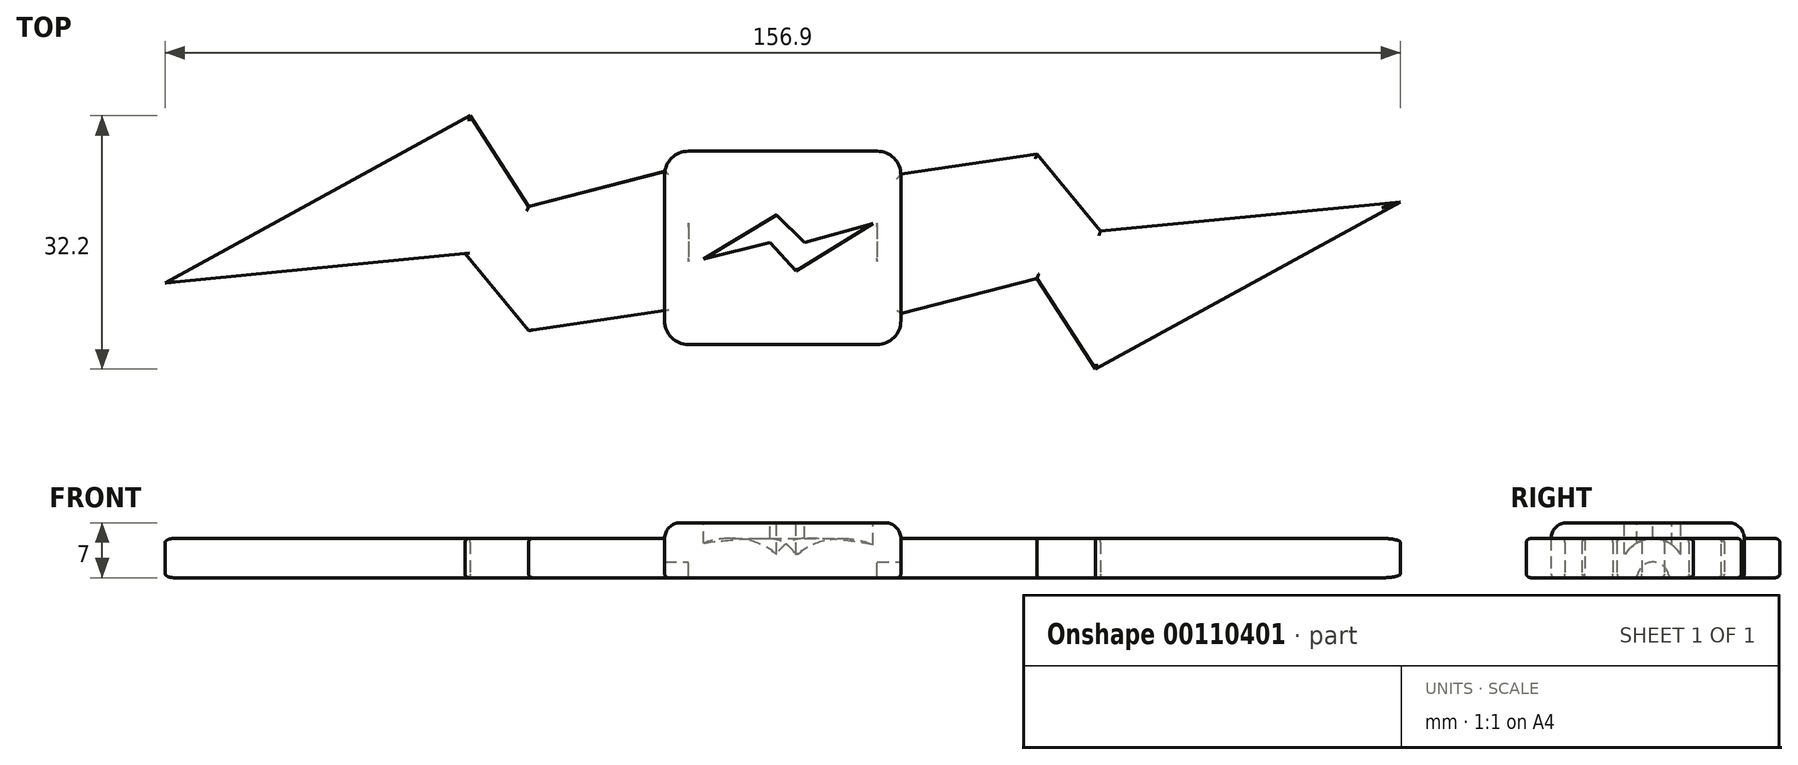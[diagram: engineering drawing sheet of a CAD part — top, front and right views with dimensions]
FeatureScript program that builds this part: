
annotation { "Feature Type Name" : "Feature", "Feature Type Description" : "" }
export const myFeature = defineFeature(function(context is Context, id is Id, definition is map)
    precondition{}
    {
        {
            var Q0;
            Q0=qCreatedBy(makeId("Top.planeOp"),FACE);
            var sketch = newSketch(context, id + "F0", { "sketchPlane" : qUnion([Q0])});
            skLineSegment(sketch, "E0.bottom", {"start": v(0, 11.6) * mm, "end": v(-15, 11.6) * mm});
            skLineSegment(sketch, "E0.top", {"start": v(0, -12.95) * mm, "end": v(-15, -12.95) * mm});
            skLineSegment(sketch, "E0.left", {"start": v(0, 11.6) * mm, "end": v(0, -12.95) * mm});
            skLineSegment(sketch, "E0.right", {"start": v(-15, 11.6) * mm, "end": v(-15, -12.95) * mm});
            skLineSegment(sketch, "E1", {"start": v(-78.45, -5.13) * mm, "end": v(-39.7, 16.1) * mm});
            skLineSegment(sketch, "E2", {"start": v(-39.7, 16.1) * mm, "end": v(-32.29, 4.57) * mm});
            skLineSegment(sketch, "E3", {"start": v(-32.29, 4.57) * mm, "end": v(-15, 9.02) * mm});
            skLineSegment(sketch, "E4", {"start": v(-15, 11.6) * mm, "end": v(-15, 9.02) * mm});
            skLineSegment(sketch, "E5", {"start": v(-78.45, -5.13) * mm, "end": v(-40.38, -1.43) * mm});
            skLineSegment(sketch, "E6", {"start": v(-40.38, -1.43) * mm, "end": v(-32.29, -11.2) * mm});
            skLineSegment(sketch, "E7", {"start": v(-32.29, -11.2) * mm, "end": v(-15, -8.67) * mm});
            skLineSegment(sketch, "E8.MirrorCS", {"start": v(0, -12.95) * mm, "end": v(15, -12.95) * mm});
            skLineSegment(sketch, "E9.MirrorCS", {"start": v(15, 11.6) * mm, "end": v(15, -12.95) * mm});
            skLineSegment(sketch, "E10", {"start": v(0, 0) * mm, "end": v(18.95, 0) * mm, "construction": true});
            skLineSegment(sketch, "E11.MirrorCS", {"start": v(40.38, 1.43) * mm, "end": v(32.29, 11.2) * mm});
            skLineSegment(sketch, "E12.MirrorCS", {"start": v(78.45, 5.13) * mm, "end": v(40.38, 1.43) * mm});
            skLineSegment(sketch, "E13.MirrorCS", {"start": v(32.29, -4.57) * mm, "end": v(15, -9.02) * mm});
            skLineSegment(sketch, "E14.MirrorCS", {"start": v(39.7, -16.1) * mm, "end": v(32.29, -4.57) * mm});
            skLineSegment(sketch, "E15.MirrorCS", {"start": v(78.45, 5.13) * mm, "end": v(39.7, -16.1) * mm});
            skLineSegment(sketch, "E16.MirrorCS", {"start": v(32.29, 11.2) * mm, "end": v(15, 8.67) * mm});
            skLineSegment(sketch, "E17", {"start": v(0, 11.6) * mm, "end": v(15, 11.6) * mm});
            skSolve(sketch);
        }
        {
            var Q0;
            Q0 = qSketchRegion(id + "F0", true);
            extrude(context, id + "F1", {"entities" : qUnion([Q0]), "depth" : 5 * mm});
        }
        {
            var Q0;
            Q0=makeQuery(id+"F1.opExtrude","CAP_FACE",FACE,{"disambiguationData":[OSD([sQuery(id+"F0.wireOp",EDGE,"E8.MirrorCS"),sQuery(id+"F0.wireOp",EDGE,"E9.MirrorCS"),sQuery(id+"F0.wireOp",EDGE,"E6"),sQuery(id+"F0.wireOp",EDGE,"E5"),sQuery(id+"F0.wireOp",EDGE,"E3"),sQuery(id+"F0.wireOp",EDGE,"E0.bottom"),sQuery(id+"F0.wireOp",EDGE,"E0.right"),sQuery(id+"F0.wireOp",EDGE,"E7"),sQuery(id+"F0.wireOp",EDGE,"E2"),sQuery(id+"F0.wireOp",EDGE,"E0.top"),sQuery(id+"F0.wireOp",EDGE,"E1"),sQuery(id+"F0.wireOp",EDGE,"E11.MirrorCS"),sQuery(id+"F0.wireOp",EDGE,"E12.MirrorCS"),sQuery(id+"F0.wireOp",EDGE,"E13.MirrorCS"),sQuery(id+"F0.wireOp",EDGE,"E14.MirrorCS"),sQuery(id+"F0.wireOp",EDGE,"E15.MirrorCS"),sQuery(id+"F0.wireOp",EDGE,"E16.MirrorCS"),sQuery(id+"F0.wireOp",EDGE,"E17")])],"isStart":false});
            var sketch = newSketch(context, id + "F2", { "sketchPlane" : qUnion([Q0])});
            skLineSegment(sketch, "E18.bottom", {"start": v(-15, 11.6) * mm, "end": v(15, 11.6) * mm});
            skLineSegment(sketch, "E18.top", {"start": v(-15, -12.95) * mm, "end": v(15, -12.95) * mm});
            skLineSegment(sketch, "E18.left", {"start": v(-15, 11.6) * mm, "end": v(-15, -12.95) * mm});
            skLineSegment(sketch, "E18.right", {"start": v(15, 11.6) * mm, "end": v(15, -12.95) * mm});
            skSolve(sketch);
        }
        {
            var Q0;
            Q0 = qSketchRegion(id + "F2", true);
            extrude(context, id + "F3", {"entities" : qUnion([Q0]), "operationType" : NewBodyOperationType.ADD, "depth" : 2 * mm});
        }
        {
            var Q0;
            Q0=makeQuery(id+"F3.boolean.opBoolean","MERGE",EDGE,{"derivedFrom":[makeQuery(id+"F1.opExtrude","SWEPT_EDGE",EDGE,{"disambiguationData":[OSD([sQuery(id+"F0.wireOp",EDGE,"E0.bottom"),sQuery(id+"F0.wireOp",EDGE,"E0.right")])]}),makeQuery(id+"F3.opExtrude","SWEPT_EDGE",EDGE,{"disambiguationData":[OSD([sQuery(id+"F2.wireOp",EDGE,"E18.bottom"),sQuery(id+"F2.wireOp",EDGE,"E18.left")])]})]});
            var Q1;
            Q1=makeQuery(id+"F3.boolean.opBoolean","MERGE",EDGE,{"derivedFrom":[makeQuery(id+"F1.opExtrude","SWEPT_EDGE",EDGE,{"disambiguationData":[OSD([sQuery(id+"F0.wireOp",EDGE,"E9.MirrorCS"),sQuery(id+"F0.wireOp",EDGE,"E17")])]}),makeQuery(id+"F3.opExtrude","SWEPT_EDGE",EDGE,{"disambiguationData":[OSD([sQuery(id+"F2.wireOp",EDGE,"E18.bottom"),sQuery(id+"F2.wireOp",EDGE,"E18.right")])]})]});
            var Q2;
            Q2=makeQuery(id+"F3.boolean.opBoolean","MERGE",EDGE,{"derivedFrom":[makeQuery(id+"F1.opExtrude","SWEPT_EDGE",EDGE,{"disambiguationData":[OSD([sQuery(id+"F0.wireOp",EDGE,"E0.right"),sQuery(id+"F0.wireOp",EDGE,"E0.top")])]}),makeQuery(id+"F3.opExtrude","SWEPT_EDGE",EDGE,{"disambiguationData":[OSD([sQuery(id+"F2.wireOp",EDGE,"E18.top"),sQuery(id+"F2.wireOp",EDGE,"E18.left")])]})]});
            var Q3;
            Q3=makeQuery(id+"F3.boolean.opBoolean","MERGE",EDGE,{"derivedFrom":[makeQuery(id+"F1.opExtrude","SWEPT_EDGE",EDGE,{"disambiguationData":[OSD([sQuery(id+"F0.wireOp",EDGE,"E8.MirrorCS"),sQuery(id+"F0.wireOp",EDGE,"E9.MirrorCS")])]}),makeQuery(id+"F3.opExtrude","SWEPT_EDGE",EDGE,{"disambiguationData":[OSD([sQuery(id+"F2.wireOp",EDGE,"E18.top"),sQuery(id+"F2.wireOp",EDGE,"E18.right")])]})]});
            fillet(context, id + "F4", {"entities" : qUnion([Q0, Q1, Q2, Q3]), "radius" : 3 * mm, "tangentPropagation" : true, "allowEdgeOverflow" : false});
        }
        {
            var Q0;
            Q0=makeQuery(id+"F3.opExtrude","CAP_EDGE",EDGE,{"disambiguationData":[OSD([sQuery(id+"F2.wireOp",EDGE,"E18.bottom")])],"isStart":false});
            fillet(context, id + "F5", {"entities" : qUnion([Q0]), "radius" : 2 * mm, "tangentPropagation" : true, "allowEdgeOverflow" : false});
        }
        {
            var Q0;
            Q0=makeQuery(id+"F3.opExtrude","CAP_FACE",FACE,{"disambiguationData":[OSD([sQuery(id+"F2.wireOp",EDGE,"E18.bottom"),sQuery(id+"F2.wireOp",EDGE,"E18.top"),sQuery(id+"F2.wireOp",EDGE,"E18.left"),sQuery(id+"F2.wireOp",EDGE,"E18.right")])],"isStart":false});
            var sketch = newSketch(context, id + "F6", { "sketchPlane" : qUnion([Q0])});
            skLineSegment(sketch, "E19", {"start": v(-10.1, -2.1) * mm, "end": v(-0.82, 3.5) * mm});
            skLineSegment(sketch, "E20", {"start": v(-0.82, 3.5) * mm, "end": v(2.75, 0) * mm});
            skLineSegment(sketch, "E21", {"start": v(2.75, 0) * mm, "end": v(11.47, 2.4) * mm});
            skLineSegment(sketch, "E22", {"start": v(11.47, 2.4) * mm, "end": v(1.7, -3.63) * mm});
            skLineSegment(sketch, "E23", {"start": v(1.7, -3.63) * mm, "end": v(-1.64, 0) * mm});
            skLineSegment(sketch, "E24", {"start": v(-1.64, 0) * mm, "end": v(-10.1, -2.1) * mm});
            skSolve(sketch);
        }
        {
            var Q0;
            Q0 = qSketchRegion(id + "F6", true);
            extrude(context, id + "F7", {"entities" : qUnion([Q0]), "operationType" : NewBodyOperationType.REMOVE, "oppositeDirection" : true, "depth" : 4 * mm});
        }
        {
            var Q0;
            Q0=makeQuery(id+"F1.opExtrude","CAP_FACE",FACE,{"disambiguationData":[OSD([sQuery(id+"F0.wireOp",EDGE,"E8.MirrorCS"),sQuery(id+"F0.wireOp",EDGE,"E9.MirrorCS"),sQuery(id+"F0.wireOp",EDGE,"E6"),sQuery(id+"F0.wireOp",EDGE,"E5"),sQuery(id+"F0.wireOp",EDGE,"E3"),sQuery(id+"F0.wireOp",EDGE,"E0.bottom"),sQuery(id+"F0.wireOp",EDGE,"E0.right"),sQuery(id+"F0.wireOp",EDGE,"E7"),sQuery(id+"F0.wireOp",EDGE,"E2"),sQuery(id+"F0.wireOp",EDGE,"E0.top"),sQuery(id+"F0.wireOp",EDGE,"E1"),sQuery(id+"F0.wireOp",EDGE,"E11.MirrorCS"),sQuery(id+"F0.wireOp",EDGE,"E12.MirrorCS"),sQuery(id+"F0.wireOp",EDGE,"E13.MirrorCS"),sQuery(id+"F0.wireOp",EDGE,"E14.MirrorCS"),sQuery(id+"F0.wireOp",EDGE,"E15.MirrorCS"),sQuery(id+"F0.wireOp",EDGE,"E16.MirrorCS"),sQuery(id+"F0.wireOp",EDGE,"E17")])],"isStart":true});
            var sketch = newSketch(context, id + "F8", { "sketchPlane" : qUnion([Q0])});
            skLineSegment(sketch, "E25.bottom", {"start": v(15, -4) * mm, "end": v(12, -4) * mm});
            skLineSegment(sketch, "E25.top", {"start": v(15, 4) * mm, "end": v(12, 4) * mm});
            skLineSegment(sketch, "E25.left", {"start": v(15, -4) * mm, "end": v(15, 4) * mm});
            skLineSegment(sketch, "E25.right", {"start": v(12, -4) * mm, "end": v(12, 4) * mm});
            skLineSegment(sketch, "E26", {"start": v(0, 0) * mm, "end": v(0, -6.2) * mm, "construction": true});
            skLineSegment(sketch, "E27.MirrorCS", {"start": v(-15, -4) * mm, "end": v(-12, -4) * mm});
            skLineSegment(sketch, "E28.MirrorCS", {"start": v(-15, -4) * mm, "end": v(-15, 4) * mm});
            skLineSegment(sketch, "E29.MirrorCS", {"start": v(-12, -4) * mm, "end": v(-12, 4) * mm});
            skLineSegment(sketch, "E30.MirrorCS", {"start": v(-15, 4) * mm, "end": v(-12, 4) * mm});
            skSolve(sketch);
        }
        {
            var Q0;
            Q0 = qSketchRegion(id + "F8", true);
            extrude(context, id + "F9", {"entities" : qUnion([Q0]), "operationType" : NewBodyOperationType.REMOVE, "oppositeDirection" : true, "depth" : 5 * mm});
        }
        {
            var Q0;
            Q0=makeQuery(id+"F9.boolean.opBoolean","COPY",EDGE,{"derivedFrom":makeQuery(id+"F9.opExtrude","CAP_EDGE",EDGE,{"disambiguationData":[OSD([sQuery(id+"F8.wireOp",EDGE,"E25.bottom")])],"isStart":false})});
            var Q1;
            Q1=makeQuery(id+"F9.boolean.opBoolean","COPY",EDGE,{"derivedFrom":makeQuery(id+"F9.opExtrude","CAP_EDGE",EDGE,{"disambiguationData":[OSD([sQuery(id+"F8.wireOp",EDGE,"E25.top")])],"isStart":false})});
            var Q2;
            Q2=makeQuery(id+"F9.boolean.opBoolean","COPY",EDGE,{"derivedFrom":makeQuery(id+"F9.opExtrude","CAP_EDGE",EDGE,{"disambiguationData":[OSD([sQuery(id+"F8.wireOp",EDGE,"E30.MirrorCS")])],"isStart":false})});
            var Q3;
            Q3=makeQuery(id+"F9.boolean.opBoolean","COPY",EDGE,{"derivedFrom":makeQuery(id+"F9.opExtrude","CAP_EDGE",EDGE,{"disambiguationData":[OSD([sQuery(id+"F8.wireOp",EDGE,"E27.MirrorCS")])],"isStart":false})});
            fillet(context, id + "F10", {"entities" : qUnion([Q0, Q1, Q2, Q3]), "radius" : 4 * mm, "tangentPropagation" : true, "allowEdgeOverflow" : false});
        }
        {
            var Q0;
            Q0=makeQuery(id+"F9.boolean.opBoolean","COPY",FACE,{"derivedFrom":makeQuery(id+"F9.opExtrude","SWEPT_FACE",FACE,{"disambiguationData":[OSD([sQuery(id+"F8.wireOp",EDGE,"E25.left")])]})});
            var sketch = newSketch(context, id + "F11", { "sketchPlane" : qUnion([Q0])});
            skArc(sketch, "E31", {"start": v(-2, 0) * mm, "mid": v(0, 2) * mm, "end": v(2, 0) * mm});
            skSolve(sketch);
        }
        {
            var Q0;
            {var subQ0=sQuery(id+"F11.wireOp",EDGE,"E31");Q0=makeQuery(id+"F11.imprint","IMPRINT",FACE,{"disambiguationData":[TD([[makeQuery(id+"F11.imprint","IMPRINT",EDGE,{"derivedFrom":subQ0}),-1.0]])]});}
            var Q1;
            Q1=makeQuery(id+"F9.boolean.opBoolean","COPY",FACE,{"derivedFrom":makeQuery(id+"F9.opExtrude","SWEPT_FACE",FACE,{"disambiguationData":[OSD([sQuery(id+"F8.wireOp",EDGE,"E28.MirrorCS")])]})});
            extrude(context, id + "F12", {"entities" : qUnion([Q0]), "operationType" : NewBodyOperationType.ADD, "endBound" : BoundingType.UP_TO_SURFACE, "endBoundEntityFace" : qUnion([Q1]), "depth" : 25 * mm});
        }
        {
            var Q0;
            Q0=makeQuery(id+"F1.opExtrude","CAP_EDGE",EDGE,{"disambiguationData":[OSD([sQuery(id+"F0.wireOp",EDGE,"E7")])],"isStart":true});
            var Q1;
            Q1=makeQuery(id+"F1.opExtrude","CAP_EDGE",EDGE,{"disambiguationData":[OSD([sQuery(id+"F0.wireOp",EDGE,"E6")])],"isStart":true});
            var Q2;
            Q2=makeQuery(id+"F1.opExtrude","CAP_EDGE",EDGE,{"disambiguationData":[OSD([sQuery(id+"F0.wireOp",EDGE,"E5")])],"isStart":true});
            var Q3;
            Q3=makeQuery(id+"F1.opExtrude","CAP_EDGE",EDGE,{"disambiguationData":[OSD([sQuery(id+"F0.wireOp",EDGE,"E1")])],"isStart":true});
            var Q4;
            Q4=makeQuery(id+"F1.opExtrude","CAP_EDGE",EDGE,{"disambiguationData":[OSD([sQuery(id+"F0.wireOp",EDGE,"E2")])],"isStart":true});
            var Q5;
            Q5=makeQuery(id+"F1.opExtrude","CAP_EDGE",EDGE,{"disambiguationData":[OSD([sQuery(id+"F0.wireOp",EDGE,"E3")])],"isStart":true});
            var Q6;
            Q6=makeQuery(id+"F1.opExtrude","CAP_EDGE",EDGE,{"disambiguationData":[OSD([sQuery(id+"F0.wireOp",EDGE,"E8.MirrorCS"),sQuery(id+"F0.wireOp",EDGE,"E0.top")])],"isStart":true});
            var Q7;
            Q7=makeQuery(id+"F1.opExtrude","CAP_EDGE",EDGE,{"disambiguationData":[OSD([sQuery(id+"F0.wireOp",EDGE,"E0.bottom"),sQuery(id+"F0.wireOp",EDGE,"E17")])],"isStart":true});
            var Q8;
            Q8=makeQuery(id+"F1.opExtrude","CAP_EDGE",EDGE,{"disambiguationData":[OSD([sQuery(id+"F0.wireOp",EDGE,"E13.MirrorCS")])],"isStart":true});
            var Q9;
            Q9=makeQuery(id+"F1.opExtrude","CAP_EDGE",EDGE,{"disambiguationData":[OSD([sQuery(id+"F0.wireOp",EDGE,"E16.MirrorCS")])],"isStart":true});
            var Q10;
            Q10=makeQuery(id+"F1.opExtrude","CAP_EDGE",EDGE,{"disambiguationData":[OSD([sQuery(id+"F0.wireOp",EDGE,"E14.MirrorCS")])],"isStart":true});
            var Q11;
            Q11=makeQuery(id+"F1.opExtrude","CAP_EDGE",EDGE,{"disambiguationData":[OSD([sQuery(id+"F0.wireOp",EDGE,"E11.MirrorCS")])],"isStart":true});
            var Q12;
            Q12=makeQuery(id+"F1.opExtrude","CAP_EDGE",EDGE,{"disambiguationData":[OSD([sQuery(id+"F0.wireOp",EDGE,"E15.MirrorCS")])],"isStart":true});
            var Q13;
            Q13=makeQuery(id+"F1.opExtrude","CAP_EDGE",EDGE,{"disambiguationData":[OSD([sQuery(id+"F0.wireOp",EDGE,"E12.MirrorCS")])],"isStart":true});
            fillet(context, id + "F13", {"entities" : qUnion([Q0, Q1, Q2, Q3, Q4, Q5, Q6, Q7, Q8, Q9, Q10, Q11, Q12, Q13]), "radius" : 0.5 * mm, "tangentPropagation" : true, "allowEdgeOverflow" : false});
        }
        {
            var Q0;
            {var subQ0=sQuery(id+"F8.wireOp",EDGE,"E28.MirrorCS");Q0=makeQuery(id+"F12.boolean.opBoolean","SPLIT",EDGE,{"disambiguationData":[TD([makeQuery(id+"F9.boolean.opBoolean","COPY",FACE,{"derivedFrom":makeQuery(id+"F9.opExtrude","SWEPT_FACE",FACE,{"disambiguationData":[OSD([sQuery(id+"F8.wireOp",EDGE,"E30.MirrorCS")])]})})])],"derivedFrom":makeQuery(id+"F9.boolean.opBoolean","COPY",EDGE,{"derivedFrom":makeQuery(id+"F9.opExtrude","CAP_EDGE",EDGE,{"disambiguationData":[OSD([subQ0])],"isStart":true})})});}
            var Q1;
            {var subQ0=sQuery(id+"F11.wireOp",EDGE,"E31");var subQ1=sQuery(id+"F8.wireOp",EDGE,"E25.left");Q1=makeQuery(id+"F12.boolean.opBoolean","SPLIT",EDGE,{"disambiguationData":[TD([makeQuery(id+"F9.boolean.opBoolean","COPY",FACE,{"derivedFrom":makeQuery(id+"F9.opExtrude","SWEPT_FACE",FACE,{"disambiguationData":[OSD([sQuery(id+"F8.wireOp",EDGE,"E28.MirrorCS")])]})})])],"derivedFrom":makeQuery(id+"F12.opExtrude","SWEPT_EDGE",EDGE,{"disambiguationData":[OSD([subQ1,subQ0]),TDD([makeQuery(id+"F11.imprint","INTERSECT",VERTEX,{"disambiguationData":[OD(1.0)],"derivedFrom":[makeQuery(id+"F9.boolean.opBoolean","COPY",EDGE,{"derivedFrom":makeQuery(id+"F9.opExtrude","CAP_EDGE",EDGE,{"disambiguationData":[OSD([subQ1])],"isStart":true})}),subQ0]})])]})});}
            var Q2;
            {var subQ0=sQuery(id+"F8.wireOp",EDGE,"E29.MirrorCS");Q2=makeQuery(id+"F12.boolean.opBoolean","SPLIT",EDGE,{"disambiguationData":[TD([makeQuery(id+"F9.boolean.opBoolean","COPY",FACE,{"derivedFrom":makeQuery(id+"F9.opExtrude","SWEPT_FACE",FACE,{"disambiguationData":[OSD([sQuery(id+"F8.wireOp",EDGE,"E30.MirrorCS")])]})})])],"derivedFrom":makeQuery(id+"F9.boolean.opBoolean","COPY",EDGE,{"derivedFrom":makeQuery(id+"F9.opExtrude","CAP_EDGE",EDGE,{"disambiguationData":[OSD([subQ0])],"isStart":true})})});}
            var Q3;
            Q3=makeQuery(id+"F9.boolean.opBoolean","COPY",EDGE,{"derivedFrom":makeQuery(id+"F9.opExtrude","CAP_EDGE",EDGE,{"disambiguationData":[OSD([sQuery(id+"F8.wireOp",EDGE,"E30.MirrorCS")])],"isStart":true})});
            var Q4;
            {var subQ0=sQuery(id+"F11.wireOp",EDGE,"E31");var subQ1=sQuery(id+"F8.wireOp",EDGE,"E25.left");Q4=makeQuery(id+"F12.boolean.opBoolean","SPLIT",EDGE,{"disambiguationData":[TD([makeQuery(id+"F9.boolean.opBoolean","COPY",FACE,{"derivedFrom":makeQuery(id+"F9.opExtrude","SWEPT_FACE",FACE,{"disambiguationData":[OSD([sQuery(id+"F8.wireOp",EDGE,"E28.MirrorCS")])]})})])],"derivedFrom":makeQuery(id+"F12.opExtrude","SWEPT_EDGE",EDGE,{"disambiguationData":[OSD([subQ1,subQ0]),TDD([makeQuery(id+"F11.imprint","INTERSECT",VERTEX,{"disambiguationData":[OD(0.0)],"derivedFrom":[makeQuery(id+"F9.boolean.opBoolean","COPY",EDGE,{"derivedFrom":makeQuery(id+"F9.opExtrude","CAP_EDGE",EDGE,{"disambiguationData":[OSD([subQ1])],"isStart":true})}),subQ0]})])]})});}
            var Q5;
            {var subQ0=sQuery(id+"F8.wireOp",EDGE,"E28.MirrorCS");Q5=makeQuery(id+"F12.boolean.opBoolean","SPLIT",EDGE,{"disambiguationData":[TD([makeQuery(id+"F9.boolean.opBoolean","COPY",FACE,{"derivedFrom":makeQuery(id+"F9.opExtrude","SWEPT_FACE",FACE,{"disambiguationData":[OSD([sQuery(id+"F8.wireOp",EDGE,"E27.MirrorCS")])]})})])],"derivedFrom":makeQuery(id+"F9.boolean.opBoolean","COPY",EDGE,{"derivedFrom":makeQuery(id+"F9.opExtrude","CAP_EDGE",EDGE,{"disambiguationData":[OSD([subQ0])],"isStart":true})})});}
            var Q6;
            Q6=makeQuery(id+"F9.boolean.opBoolean","COPY",EDGE,{"derivedFrom":makeQuery(id+"F9.opExtrude","CAP_EDGE",EDGE,{"disambiguationData":[OSD([sQuery(id+"F8.wireOp",EDGE,"E27.MirrorCS")])],"isStart":true})});
            var Q7;
            {var subQ0=sQuery(id+"F8.wireOp",EDGE,"E29.MirrorCS");Q7=makeQuery(id+"F12.boolean.opBoolean","SPLIT",EDGE,{"disambiguationData":[TD([makeQuery(id+"F9.boolean.opBoolean","COPY",FACE,{"derivedFrom":makeQuery(id+"F9.opExtrude","SWEPT_FACE",FACE,{"disambiguationData":[OSD([sQuery(id+"F8.wireOp",EDGE,"E27.MirrorCS")])]})})])],"derivedFrom":makeQuery(id+"F9.boolean.opBoolean","COPY",EDGE,{"derivedFrom":makeQuery(id+"F9.opExtrude","CAP_EDGE",EDGE,{"disambiguationData":[OSD([subQ0])],"isStart":true})})});}
            var Q8;
            {var subQ0=sQuery(id+"F11.wireOp",EDGE,"E31");var subQ1=sQuery(id+"F8.wireOp",EDGE,"E25.left");Q8=makeQuery(id+"F12.boolean.opBoolean","SPLIT",EDGE,{"disambiguationData":[TD([makeQuery(id+"F9.boolean.opBoolean","COPY",FACE,{"derivedFrom":makeQuery(id+"F9.opExtrude","SWEPT_FACE",FACE,{"disambiguationData":[OSD([subQ1])]})})])],"derivedFrom":makeQuery(id+"F12.opExtrude","SWEPT_EDGE",EDGE,{"disambiguationData":[OSD([subQ1,subQ0]),TDD([makeQuery(id+"F11.imprint","INTERSECT",VERTEX,{"disambiguationData":[OD(1.0)],"derivedFrom":[makeQuery(id+"F9.boolean.opBoolean","COPY",EDGE,{"derivedFrom":makeQuery(id+"F9.opExtrude","CAP_EDGE",EDGE,{"disambiguationData":[OSD([subQ1])],"isStart":true})}),subQ0]})])]})});}
            var Q9;
            {var subQ0=sQuery(id+"F8.wireOp",EDGE,"E25.right");Q9=makeQuery(id+"F12.boolean.opBoolean","SPLIT",EDGE,{"disambiguationData":[TD([makeQuery(id+"F9.boolean.opBoolean","COPY",FACE,{"derivedFrom":makeQuery(id+"F9.opExtrude","SWEPT_FACE",FACE,{"disambiguationData":[OSD([sQuery(id+"F8.wireOp",EDGE,"E25.top")])]})})])],"derivedFrom":makeQuery(id+"F9.boolean.opBoolean","COPY",EDGE,{"derivedFrom":makeQuery(id+"F9.opExtrude","CAP_EDGE",EDGE,{"disambiguationData":[OSD([subQ0])],"isStart":true})})});}
            var Q10;
            Q10=makeQuery(id+"F9.boolean.opBoolean","COPY",EDGE,{"derivedFrom":makeQuery(id+"F9.opExtrude","CAP_EDGE",EDGE,{"disambiguationData":[OSD([sQuery(id+"F8.wireOp",EDGE,"E25.top")])],"isStart":true})});
            var Q11;
            {var subQ0=sQuery(id+"F8.wireOp",EDGE,"E25.left");Q11=makeQuery(id+"F12.boolean.opBoolean","SPLIT",EDGE,{"disambiguationData":[TD([makeQuery(id+"F9.boolean.opBoolean","COPY",FACE,{"derivedFrom":makeQuery(id+"F9.opExtrude","SWEPT_FACE",FACE,{"disambiguationData":[OSD([sQuery(id+"F8.wireOp",EDGE,"E25.top")])]})})])],"derivedFrom":makeQuery(id+"F9.boolean.opBoolean","COPY",EDGE,{"derivedFrom":makeQuery(id+"F9.opExtrude","CAP_EDGE",EDGE,{"disambiguationData":[OSD([subQ0])],"isStart":true})})});}
            var Q12;
            {var subQ0=sQuery(id+"F8.wireOp",EDGE,"E25.left");Q12=makeQuery(id+"F12.boolean.opBoolean","SPLIT",EDGE,{"disambiguationData":[TD([makeQuery(id+"F9.boolean.opBoolean","COPY",FACE,{"derivedFrom":makeQuery(id+"F9.opExtrude","SWEPT_FACE",FACE,{"disambiguationData":[OSD([sQuery(id+"F8.wireOp",EDGE,"E25.bottom")])]})})])],"derivedFrom":makeQuery(id+"F9.boolean.opBoolean","COPY",EDGE,{"derivedFrom":makeQuery(id+"F9.opExtrude","CAP_EDGE",EDGE,{"disambiguationData":[OSD([subQ0])],"isStart":true})})});}
            var Q13;
            {var subQ0=sQuery(id+"F11.wireOp",EDGE,"E31");var subQ1=sQuery(id+"F8.wireOp",EDGE,"E25.left");Q13=makeQuery(id+"F12.boolean.opBoolean","SPLIT",EDGE,{"disambiguationData":[TD([makeQuery(id+"F9.boolean.opBoolean","COPY",FACE,{"derivedFrom":makeQuery(id+"F9.opExtrude","SWEPT_FACE",FACE,{"disambiguationData":[OSD([subQ1])]})})])],"derivedFrom":makeQuery(id+"F12.opExtrude","SWEPT_EDGE",EDGE,{"disambiguationData":[OSD([subQ1,subQ0]),TDD([makeQuery(id+"F11.imprint","INTERSECT",VERTEX,{"disambiguationData":[OD(0.0)],"derivedFrom":[makeQuery(id+"F9.boolean.opBoolean","COPY",EDGE,{"derivedFrom":makeQuery(id+"F9.opExtrude","CAP_EDGE",EDGE,{"disambiguationData":[OSD([subQ1])],"isStart":true})}),subQ0]})])]})});}
            var Q14;
            {var subQ0=sQuery(id+"F8.wireOp",EDGE,"E25.right");Q14=makeQuery(id+"F12.boolean.opBoolean","SPLIT",EDGE,{"disambiguationData":[TD([makeQuery(id+"F9.boolean.opBoolean","COPY",FACE,{"derivedFrom":makeQuery(id+"F9.opExtrude","SWEPT_FACE",FACE,{"disambiguationData":[OSD([sQuery(id+"F8.wireOp",EDGE,"E25.bottom")])]})})])],"derivedFrom":makeQuery(id+"F9.boolean.opBoolean","COPY",EDGE,{"derivedFrom":makeQuery(id+"F9.opExtrude","CAP_EDGE",EDGE,{"disambiguationData":[OSD([subQ0])],"isStart":true})})});}
            var Q15;
            Q15=makeQuery(id+"F9.boolean.opBoolean","COPY",EDGE,{"derivedFrom":makeQuery(id+"F9.opExtrude","CAP_EDGE",EDGE,{"disambiguationData":[OSD([sQuery(id+"F8.wireOp",EDGE,"E25.bottom")])],"isStart":true})});
            fillet(context, id + "F14", {"entities" : qUnion([Q0, Q1, Q2, Q3, Q4, Q5, Q6, Q7, Q8, Q9, Q10, Q11, Q12, Q13, Q14, Q15]), "radius" : 0.5 * mm, "tangentPropagation" : true, "allowEdgeOverflow" : false});
        }
        {
            var Q0;
            Q0=makeQuery(id+"F1.opExtrude","CAP_EDGE",EDGE,{"disambiguationData":[OSD([sQuery(id+"F0.wireOp",EDGE,"E1")])],"isStart":false});
            var Q1;
            Q1=makeQuery(id+"F1.opExtrude","CAP_EDGE",EDGE,{"disambiguationData":[OSD([sQuery(id+"F0.wireOp",EDGE,"E5")])],"isStart":false});
            var Q2;
            Q2=makeQuery(id+"F1.opExtrude","CAP_EDGE",EDGE,{"disambiguationData":[OSD([sQuery(id+"F0.wireOp",EDGE,"E2")])],"isStart":false});
            var Q3;
            Q3=makeQuery(id+"F1.opExtrude","CAP_EDGE",EDGE,{"disambiguationData":[OSD([sQuery(id+"F0.wireOp",EDGE,"E6")])],"isStart":false});
            var Q4;
            Q4=makeQuery(id+"F1.opExtrude","CAP_EDGE",EDGE,{"disambiguationData":[OSD([sQuery(id+"F0.wireOp",EDGE,"E3")])],"isStart":false});
            var Q5;
            Q5=makeQuery(id+"F1.opExtrude","CAP_EDGE",EDGE,{"disambiguationData":[OSD([sQuery(id+"F0.wireOp",EDGE,"E7")])],"isStart":false});
            var Q6;
            Q6=makeQuery(id+"F1.opExtrude","CAP_EDGE",EDGE,{"disambiguationData":[OSD([sQuery(id+"F0.wireOp",EDGE,"E16.MirrorCS")])],"isStart":false});
            var Q7;
            Q7=makeQuery(id+"F1.opExtrude","CAP_EDGE",EDGE,{"disambiguationData":[OSD([sQuery(id+"F0.wireOp",EDGE,"E13.MirrorCS")])],"isStart":false});
            var Q8;
            Q8=makeQuery(id+"F1.opExtrude","CAP_EDGE",EDGE,{"disambiguationData":[OSD([sQuery(id+"F0.wireOp",EDGE,"E11.MirrorCS")])],"isStart":false});
            var Q9;
            Q9=makeQuery(id+"F1.opExtrude","CAP_EDGE",EDGE,{"disambiguationData":[OSD([sQuery(id+"F0.wireOp",EDGE,"E14.MirrorCS")])],"isStart":false});
            var Q10;
            Q10=makeQuery(id+"F1.opExtrude","CAP_EDGE",EDGE,{"disambiguationData":[OSD([sQuery(id+"F0.wireOp",EDGE,"E12.MirrorCS")])],"isStart":false});
            var Q11;
            Q11=makeQuery(id+"F1.opExtrude","CAP_EDGE",EDGE,{"disambiguationData":[OSD([sQuery(id+"F0.wireOp",EDGE,"E15.MirrorCS")])],"isStart":false});
            fillet(context, id + "F15", {"entities" : qUnion([Q0, Q1, Q2, Q3, Q4, Q5, Q6, Q7, Q8, Q9, Q10, Q11]), "radius" : 0.5 * mm, "tangentPropagation" : true, "allowEdgeOverflow" : false});
        }
    });
